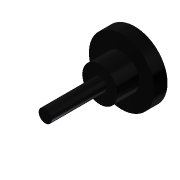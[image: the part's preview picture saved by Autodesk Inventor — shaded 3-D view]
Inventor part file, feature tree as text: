
AUTODESK INVENTOR PART (.ipt)
format: ipt  version: 2014 (Build 180170000, 170)  size: 84,480 bytes
history: native  units: mm
features: revolve x1, sketch x1
ambient origin geometry x8: Origin, YZ Plane, XZ Plane, XY Plane, X Axis, Y Axis, Z Axis, Center Point
bodies: Solid1 (feature_tree)
feature tree (2):
  revolve  "Revolution1"  [1 undecoded]
  sketch  "Sketch1"  dims[d0=15.0mm d1=6.0mm d2=10.0mm d3=8.0mm d4=25.0mm d5=3.0mm d6=90.0deg]
note: 1 required parameter value undecoded (feature->parameter linkage not recoverable at this tier; creation-order binding heuristic only, values carry confidence <= 0.55)
